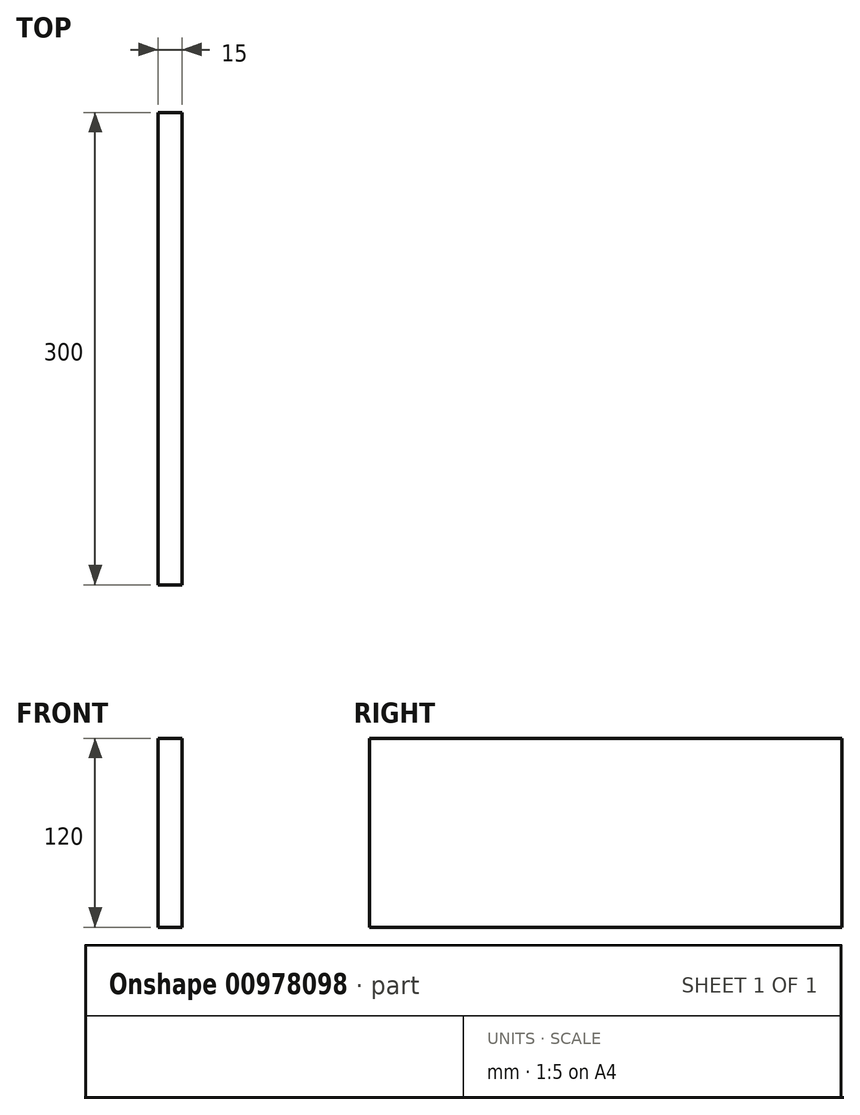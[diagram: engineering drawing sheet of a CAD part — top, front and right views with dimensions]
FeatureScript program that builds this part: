
annotation { "Feature Type Name" : "Feature", "Feature Type Description" : "" }
export const myFeature = defineFeature(function(context is Context, id is Id, definition is map)
    precondition{}
    {
        {
            var Q0;
            Q0=qCreatedBy(makeId("Right.planeOp"),FACE);
            var sketch = newSketch(context, id + "F0", { "sketchPlane" : qUnion([Q0])});
            skLineSegment(sketch, "E0.bottom", {"start": v(-150, 60) * mm, "end": v(150, 60) * mm});
            skLineSegment(sketch, "E0.top", {"start": v(-150, -60) * mm, "end": v(150, -60) * mm});
            skLineSegment(sketch, "E0.left", {"start": v(-150, 60) * mm, "end": v(-150, -60) * mm});
            skLineSegment(sketch, "E0.right", {"start": v(150, 60) * mm, "end": v(150, -60) * mm});
            skPoint(sketch, "E0.middle", {"position": v(0, 0) * mm});
            skSolve(sketch);
        }
        {
            var Q0;
            Q0 = qSketchRegion(id + "F0", true);
            extrude(context, id + "F1", {"entities" : qUnion([Q0]), "endBound" : BoundingType.SYMMETRIC, "depth" : 15 * mm, "offsetDistance" : 25 * mm});
        }
    });
